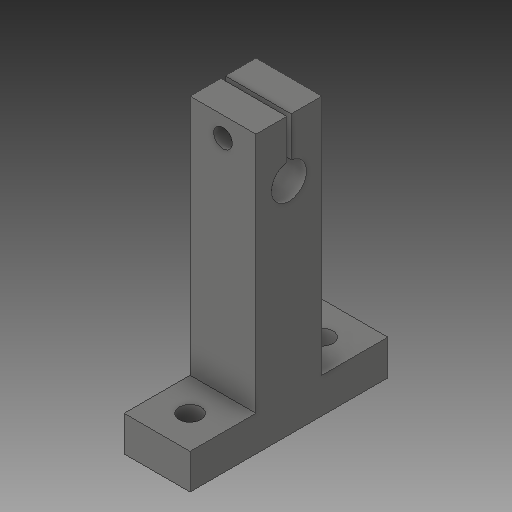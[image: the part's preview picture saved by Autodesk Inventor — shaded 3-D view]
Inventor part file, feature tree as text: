
AUTODESK INVENTOR PART (.ipt)
format: ipt  version: 2019 (Build 230136000, 136)  size: 146,944 bytes
history: native  units: mm
features: extrude x4, sketch x3, projected_geometry x2
ambient origin geometry x8: Origin, YZ Plane, XZ Plane, XY Plane, X Axis, Y Axis, Z Axis, Center Point
bodies: Solid1 (feature_tree)
feature tree (9):
  sketch  "Sketch1"  dims[d0=8.0mm d1=1.0mm]
  extrude  "Extrusion1"  Depth=1.0mm
  extrude  "Extrusion2"  Depth=15.0mm
  extrude  "Extrusion3"  Depth=8.0mm
  extrude  "Extrusion4"  Depth=15.0mm TaperAngle=0.0deg
  sketch  "Sketch2"  dims[d2=7.0mm d3=15.0mm]
  projected_geometry  "Projected Loop1"
  projected_geometry  "Projected Loop2"
  sketch  "Sketch3"  dims[d5=55.0mm d6=8.0mm d7=15.0mm d8=0.0mm d9=10.0mm d10=0.0mm d11=50.0mm d12=5.0mm d13=10.0mm d14=0.0mm d15=4.25mm d16=10.0mm d17=0.0mm]
